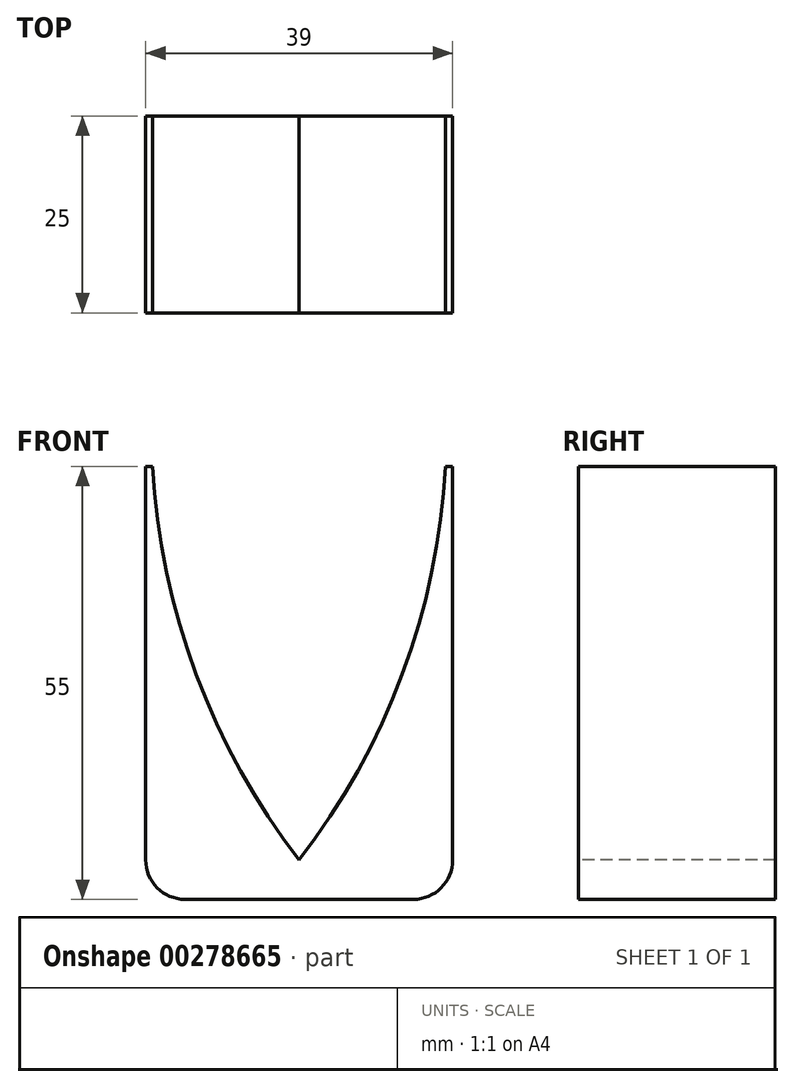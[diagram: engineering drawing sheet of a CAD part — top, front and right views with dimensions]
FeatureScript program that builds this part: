
annotation { "Feature Type Name" : "Feature", "Feature Type Description" : "" }
export const myFeature = defineFeature(function(context is Context, id is Id, definition is map)
    precondition{}
    {
        {
            var Q0;
            Q0=qCreatedBy(makeId("Front.planeOp"),FACE);
            var sketch = newSketch(context, id + "F0", { "sketchPlane" : qUnion([Q0])});
            skLineSegment(sketch, "E0.bottom", {"start": v(-19.5, -27.5) * mm, "end": v(19.5, -27.5) * mm});
            skLineSegment(sketch, "E0.top", {"start": v(-19.5, 27.5) * mm, "end": v(19.5, 27.5) * mm});
            skLineSegment(sketch, "E0.left", {"start": v(-19.5, -27.5) * mm, "end": v(-19.5, 27.5) * mm});
            skLineSegment(sketch, "E0.right", {"start": v(19.5, -27.5) * mm, "end": v(19.5, 27.5) * mm});
            skSolve(sketch);
        }
        {
            var Q0;
            Q0 = qSketchRegion(id + "F0", true);
            extrude(context, id + "F1", {"entities" : qUnion([Q0]), "depth" : 25 * mm});
        }
        {
            var Q0;
            Q0=makeQuery(id+"F1.opExtrude","CAP_FACE",FACE,{"disambiguationData":[OSD([sQuery(id+"F0.wireOp",EDGE,"E0.bottom"),sQuery(id+"F0.wireOp",EDGE,"E0.top"),sQuery(id+"F0.wireOp",EDGE,"E0.left"),sQuery(id+"F0.wireOp",EDGE,"E0.right")])],"isStart":false});
            var sketch = newSketch(context, id + "F2", { "sketchPlane" : qUnion([Q0])});
            skArc(sketch, "E1", {"start": v(-18.6, 27.5) * mm, "mid": v(-13.09, 1.1) * mm, "end": v(0, -22.5) * mm});
            skArc(sketch, "E2", {"start": v(0, -22.5) * mm, "mid": v(13.09, 1.1) * mm, "end": v(18.6, 27.5) * mm});
            skLineSegment(sketch, "E3", {"start": v(-18.6, 27.5) * mm, "end": v(18.6, 27.5) * mm});
            skSolve(sketch);
        }
        {
            var Q0;
            Q0 = qSketchRegion(id + "F2", true);
            extrude(context, id + "F3", {"entities" : qUnion([Q0]), "operationType" : NewBodyOperationType.REMOVE, "oppositeDirection" : true, "depth" : 25 * mm});
        }
        {
            var Q0;
            Q0=makeQuery(id+"F1.opExtrude","SWEPT_EDGE",EDGE,{"disambiguationData":[OSD([sQuery(id+"F0.wireOp",EDGE,"E0.bottom"),sQuery(id+"F0.wireOp",EDGE,"E0.left")])]});
            var Q1;
            Q1=makeQuery(id+"F1.opExtrude","SWEPT_EDGE",EDGE,{"disambiguationData":[OSD([sQuery(id+"F0.wireOp",EDGE,"E0.bottom"),sQuery(id+"F0.wireOp",EDGE,"E0.right")])]});
            fillet(context, id + "F4", {"entities" : qUnion([Q0, Q1]), "radius" : 5 * mm, "tangentPropagation" : true, "allowEdgeOverflow" : false});
        }
    });
